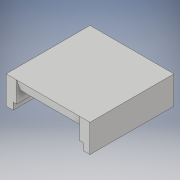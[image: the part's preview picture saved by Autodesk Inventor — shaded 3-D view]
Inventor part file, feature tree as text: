
AUTODESK INVENTOR PART (.ipt)
format: ipt  version: 2019.4 (Build 234330000, 330)  size: 123,904 bytes
history: native  units: in
note: dims shown in document units (in); Inventor stores cm internally (conversion verified against a paired STEP export)
features: extrude x3, sketch x3, chamfer x1
ambient origin geometry x8: Origin, YZ Plane, XZ Plane, XY Plane, X Axis, Y Axis, Z Axis, Center Point
bodies: Solid1 (feature_tree)
feature tree (7):
  extrude  "Extrusion1"  Depth=3.0in
  extrude  "Extrusion2"  Depth=1.0in TaperAngle=0.0deg
  extrude  "Extrusion3"  Depth=0.625in TaperAngle=0.0deg
  chamfer  "Chamfer3"  Distance=0.25in
  sketch  "Sketch1"  dims[d0=3.0in d1=1.5in]
  sketch  "Sketch2"  dims[d2=1.5in d3=1.0in d4=0.0in]
  sketch  "Sketch4"  dims[d5=1.125in d6=0.625in d7=0.0in d11=0.25in d14=0.25in d15=6.0in d16=0.0in d17=1.125in d21=0.25in d22=0.25in d23=0.375in d24=0.125in d25=45.0deg]
